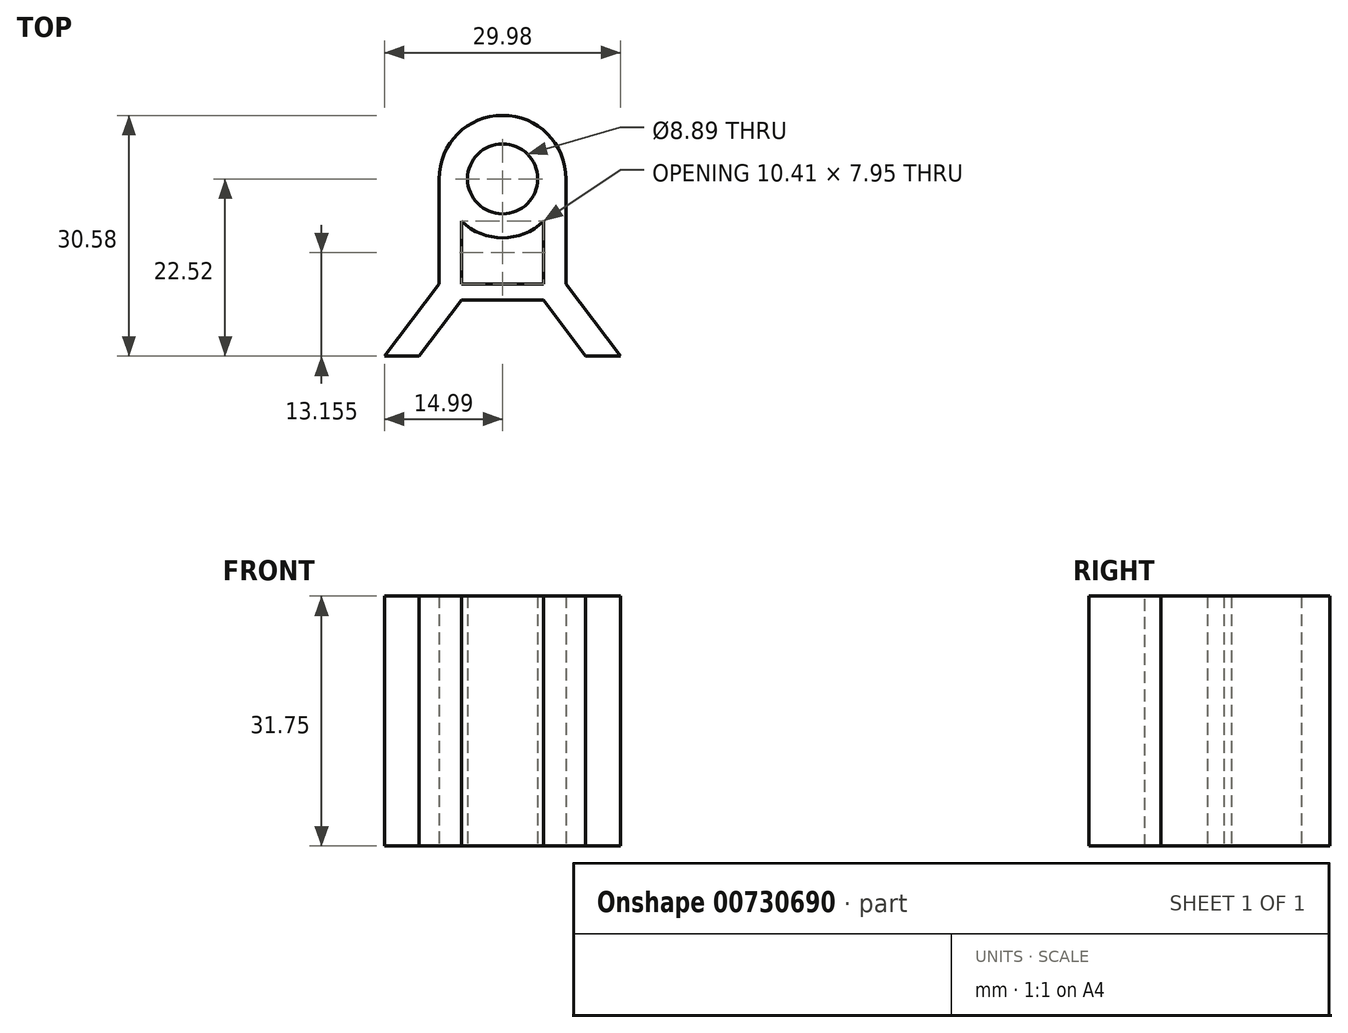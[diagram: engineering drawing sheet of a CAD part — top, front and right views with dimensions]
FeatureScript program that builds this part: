
annotation { "Feature Type Name" : "Feature", "Feature Type Description" : "" }
export const myFeature = defineFeature(function(context is Context, id is Id, definition is map)
    precondition{}
    {
        {
            var Q0;
            Q0=qCreatedBy(makeId("Top.planeOp"),FACE);
            var sketch = newSketch(context, id + "F0", { "sketchPlane" : qUnion([Q0])});
            skCircle(sketch, "E0", {"center": v(0, 0) * mm, "radius": 4.45 * mm});
            skArc(sketch, "E1", {"start": v(0, 8.06) * mm, "mid": v(-5.7, 5.7) * mm, "end": v(-8.06, 0) * mm});
            skLineSegment(sketch, "E2", {"start": v(-8.06, 0) * mm, "end": v(-8.06, -13.34) * mm});
            skLineSegment(sketch, "E3", {"start": v(-8.06, -13.34) * mm, "end": v(-14.99, -22.52) * mm});
            skLineSegment(sketch, "E4", {"start": v(-14.99, -22.52) * mm, "end": v(0, -22.52) * mm});
            skLineSegment(sketch, "E5", {"start": v(-5.2, -13.34) * mm, "end": v(-5.2, -5.39) * mm});
            skArc(sketch, "E6", {"start": v(-5.2, -5.39) * mm, "mid": v(-2.8, -6.95) * mm, "end": v(0, -7.5) * mm});
            skLineSegment(sketch, "E7", {"start": v(-5.2, -13.34) * mm, "end": v(0, -13.34) * mm});
            skArc(sketch, "E8.MirrorCS", {"start": v(0, 8.06) * mm, "mid": v(5.7, 5.7) * mm, "end": v(8.06, 0) * mm});
            skLineSegment(sketch, "E9.MirrorCS", {"start": v(5.2, -13.34) * mm, "end": v(5.2, -5.39) * mm});
            skLineSegment(sketch, "E10.MirrorCS", {"start": v(5.2, -13.34) * mm, "end": v(0, -13.34) * mm});
            skArc(sketch, "E11.MirrorCS", {"start": v(5.2, -5.39) * mm, "mid": v(2.8, -6.95) * mm, "end": v(0, -7.5) * mm});
            skLineSegment(sketch, "E12.MirrorCS", {"start": v(14.99, -22.52) * mm, "end": v(0, -22.52) * mm});
            skLineSegment(sketch, "E13.MirrorCS", {"start": v(8.06, -13.34) * mm, "end": v(14.99, -22.52) * mm});
            skLineSegment(sketch, "E14.MirrorCS", {"start": v(8.06, 0) * mm, "end": v(8.06, -13.34) * mm});
            skSolve(sketch);
        }
        {
            var Q0;
            Q0 = qSketchRegion(id + "F0", true);
            extrude(context, id + "F1", {"entities" : qUnion([Q0]), "depth" : 31.75 * mm, "offsetDistance" : 25.4 * mm});
        }
        {
            var Q0;
            Q0=makeQuery(id+"F1.opExtrude","CAP_FACE",FACE,{"disambiguationData":[OSD([sQuery(id+"F0.wireOp",EDGE,"E0"),sQuery(id+"F0.wireOp",EDGE,"E1"),sQuery(id+"F0.wireOp",EDGE,"E2"),sQuery(id+"F0.wireOp",EDGE,"E3"),sQuery(id+"F0.wireOp",EDGE,"E4"),sQuery(id+"F0.wireOp",EDGE,"E5"),sQuery(id+"F0.wireOp",EDGE,"E6"),sQuery(id+"F0.wireOp",EDGE,"E7"),sQuery(id+"F0.wireOp",EDGE,"E8.MirrorCS"),sQuery(id+"F0.wireOp",EDGE,"E9.MirrorCS"),sQuery(id+"F0.wireOp",EDGE,"E10.MirrorCS"),sQuery(id+"F0.wireOp",EDGE,"E11.MirrorCS"),sQuery(id+"F0.wireOp",EDGE,"E12.MirrorCS"),sQuery(id+"F0.wireOp",EDGE,"E13.MirrorCS"),sQuery(id+"F0.wireOp",EDGE,"E14.MirrorCS")])],"isStart":false});
            var sketch = newSketch(context, id + "F2", { "sketchPlane" : qUnion([Q0])});
            skLineSegment(sketch, "E15", {"start": v(-5.25, -15.42) * mm, "end": v(-10.6, -22.52) * mm});
            skLineSegment(sketch, "E16", {"start": v(-5.25, -15.42) * mm, "end": v(5.2, -15.42) * mm});
            skLineSegment(sketch, "E17", {"start": v(5.2, -15.42) * mm, "end": v(10.56, -22.52) * mm});
            skSolve(sketch);
        }
        {
            var Q0;
            Q0 = qSketchRegion(id + "F2", true);
            var Q1;
            {var subQ0=sQuery(id+"F2.wireOp",EDGE,"E15");Q1=makeQuery(id+"F2.imprint","IMPRINT",FACE,{"disambiguationData":[TD([[makeQuery(id+"F2.imprint","IMPRINT",EDGE,{"derivedFrom":subQ0}),1.0]])]});}
            extrude(context, id + "F3", {"entities" : qUnion([Q0, Q1]), "operationType" : NewBodyOperationType.REMOVE, "endBound" : BoundingType.THROUGH_ALL, "oppositeDirection" : true, "depth" : 25.4 * mm, "offsetDistance" : 25.4 * mm});
        }
    });
